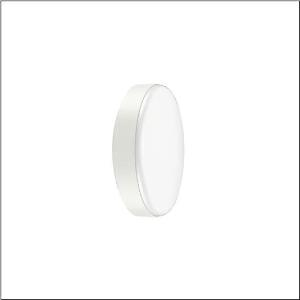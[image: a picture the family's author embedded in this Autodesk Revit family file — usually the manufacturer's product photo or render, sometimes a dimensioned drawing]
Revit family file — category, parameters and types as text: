
# Revit family: rondel_31_51wc10ma32a
name_source: partatom
category: Lighting Fixtures
units: mm (PartAtom-declared; Revit-internal decimal feet)

## family parameters
Cut with Voids When Loaded = No
Host = Face
Light Source = No
Part Type = Normal
Room Calculation Point = No
Round Connector Dimension = Use Diameter
Shared = No

## types (1)
- --- (1 x LED, 2450 lm, 19 W, 3000K)
    Apparent Load = 19 VA
    CIE Flux Codes = 44 75 94 94 100
    Color Rendering = 80
    Color Temperature = 3000K
    Default Elevation = 1800 mm
    Description = Rondel 31, wall and ceiling luminaire, primary optical cover: cover, of PC, opal, light emission: direct distribution, primary light characteristic: symmetric, installation type: surface-mounted, LED, rated luminous flux: 2.450lm, luminous efficacy: 129lm/W, light colour: 830, colour temperature: 3000K, with terminal, 3-pole, max. 2.5mm², mains connection: 220..240V, AC, 50/60Hz, rated input power: 19W, luminaire housing, of PC, traffic white (RAL 9016), diameter: 350mm, protection rating (complete): IP65, insulation class (complete): insulation class II (safety insulation), certification: CE, impact resistance: IK10, permissible operating ambient temperature: -20..+40°C, permissible storage temperature: -20..+60°C, packaging unit: 1 piece
    Height = 97 mm
    Lamp = 1 x LED
    Lamp Light Flux = 2450 lm
    Lamp Power = 19 W
    Lamp count = 1
    Length = 350 mm
    Luminous efficacy = 129 lm/W
    Manufacturer = Siteco
    ModVariant = No
    Model = 51WC10MA32A
    Mounting Place = Ceiling
    Mounting Type = Surface mounted
    Number of Poles = 1
    OnlyDefault = Yes
    Power Factor = 1
    Product Name = Rondel 31
    Product group = wall and ceiling luminaire
    ProductGroupID = 301
    Protection Class = Protection class II
    Protection Degree = IP 65
    RLX_Detail_Level = 1
    RLX_Emergency_Light_Flux = 0 lm
    RLX_Emergency_Type = 0
    RLX_Emergency_Type_DB = No
    RlxData = <blob elided: 30265 chars, md5=9158b1d3>
    Socket = socket
    Standby Power = 0 W
    System Light Flux = 2450 lm
    System Power = 19 W
    Type Comments = factory setting: luminous flux: 100 % | (ON | ON)
    Type Image = l_1007027.jpg
    URL = http://relux.com
    VarID = @adj_083051
    Voltage = 0 V
    Weight = 0.00 kg
    Width = 0 mm  [stored 0 ft]

note: [stored X ft] marks values corroborated as IEEE doubles in the binary element streams (Revit-internal decimal feet)

## geometry (parser evidence)
native form markers: Blend x4, Sweep x12
no freeform markers — native parametric forms only
